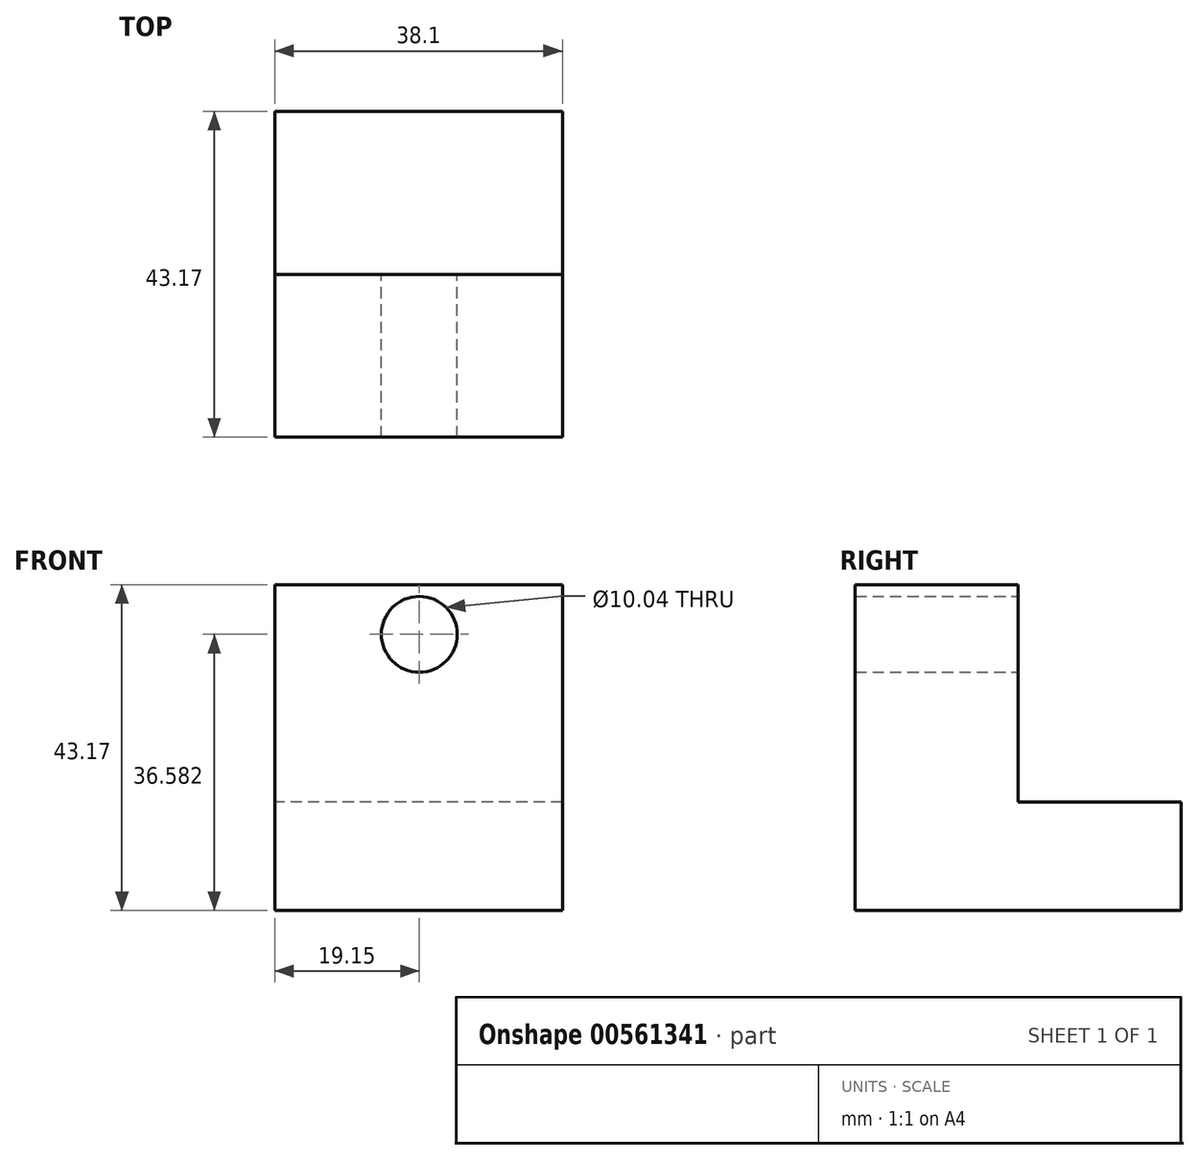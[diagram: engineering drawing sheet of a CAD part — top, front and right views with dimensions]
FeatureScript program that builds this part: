
annotation { "Feature Type Name" : "Feature", "Feature Type Description" : "" }
export const myFeature = defineFeature(function(context is Context, id is Id, definition is map)
    precondition{}
    {
        {
            var Q0;
            Q0=qCreatedBy(makeId("Right.planeOp"),FACE);
            var sketch = newSketch(context, id + "F0", { "sketchPlane" : qUnion([Q0])});
            skLineSegment(sketch, "E0", {"start": v(0, 43.17) * mm, "end": v(21.59, 43.17) * mm});
            skLineSegment(sketch, "E1", {"start": v(0, 43.17) * mm, "end": v(0, 0) * mm});
            skLineSegment(sketch, "E2", {"start": v(0, 0) * mm, "end": v(43.17, 0) * mm});
            skLineSegment(sketch, "E3", {"start": v(43.17, 0) * mm, "end": v(43.17, 14.35) * mm});
            skLineSegment(sketch, "E4", {"start": v(43.17, 14.35) * mm, "end": v(21.59, 14.35) * mm});
            skLineSegment(sketch, "E5", {"start": v(21.59, 14.35) * mm, "end": v(21.59, 43.17) * mm});
            skSolve(sketch);
        }
        {
            var Q0;
            Q0=makeQuery(id+"F0.imprint","IMPRINT",FACE,{"disambiguationData":[TD([[makeQuery(id+"F0.imprint","IMPRINT",EDGE,{"derivedFrom":sQuery(id+"F0.wireOp",EDGE,"E0")}),-1.0]])]});
            extrude(context, id + "F1", {"entities" : qUnion([Q0]), "depth" : 38.1 * mm, "offsetDistance" : 25.4 * mm});
        }
        {
            var Q0;
            Q0=makeQuery(id+"F1.opExtrude","SWEPT_FACE",FACE,{"disambiguationData":[OSD([sQuery(id+"F0.wireOp",EDGE,"E5")])]});
            var sketch = newSketch(context, id + "F2", { "sketchPlane" : qUnion([Q0])});
            skCircle(sketch, "E6", {"center": v(-19.15, 36.58) * mm, "radius": 5.02 * mm});
            skSolve(sketch);
        }
        {
            var Q0;
            Q0=makeQuery(id+"F2.imprint","IMPRINT",FACE,{"disambiguationData":[TD([[makeQuery(id+"F2.imprint","IMPRINT",EDGE,{"derivedFrom":sQuery(id+"F2.wireOp",EDGE,"E6")}),1.0]])]});
            extrude(context, id + "F3", {"entities" : qUnion([Q0]), "operationType" : NewBodyOperationType.REMOVE, "oppositeDirection" : true, "depth" : 24.13 * mm, "offsetDistance" : 25.4 * mm});
        }
    });
